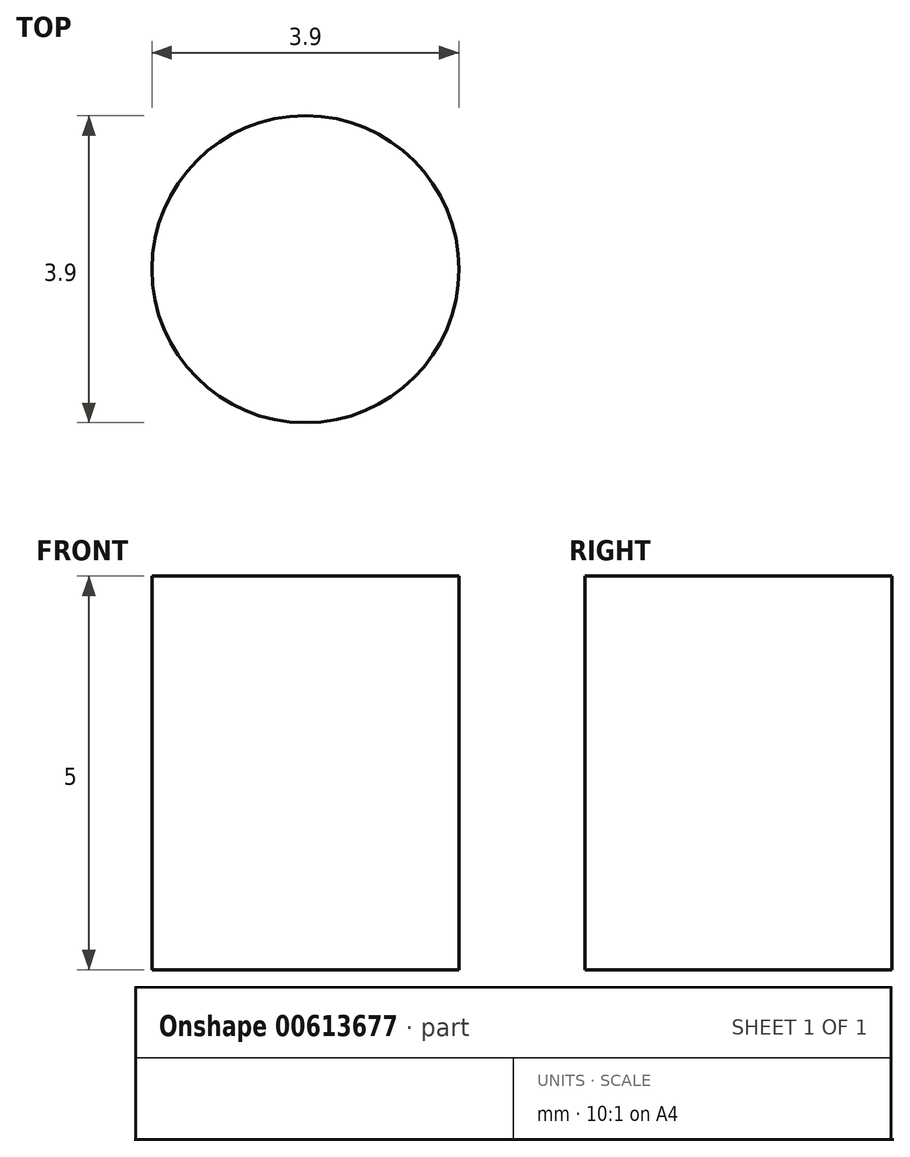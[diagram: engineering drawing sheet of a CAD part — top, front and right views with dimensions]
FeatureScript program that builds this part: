
annotation { "Feature Type Name" : "Feature", "Feature Type Description" : "" }
export const myFeature = defineFeature(function(context is Context, id is Id, definition is map)
    precondition{}
    {
        {
            var Q0;
            Q0=qCreatedBy(makeId("Top.planeOp"),FACE);
            var sketch = newSketch(context, id + "F0", { "sketchPlane" : qUnion([Q0])});
            skCircle(sketch, "E0", {"center": v(0, 0) * mm, "radius": 1.95 * mm});
            skSolve(sketch);
        }
        {
            var Q0;
            Q0=makeQuery(id+"F0.imprint","IMPRINT",FACE,{"disambiguationData":[TD([[makeQuery(id+"F0.imprint","IMPRINT",EDGE,{"derivedFrom":sQuery(id+"F0.wireOp",EDGE,"E0")}),1.0]])]});
            extrude(context, id + "F1", {"entities" : qUnion([Q0]), "depth" : 5 * mm, "offsetDistance" : 25 * mm});
        }
    });
